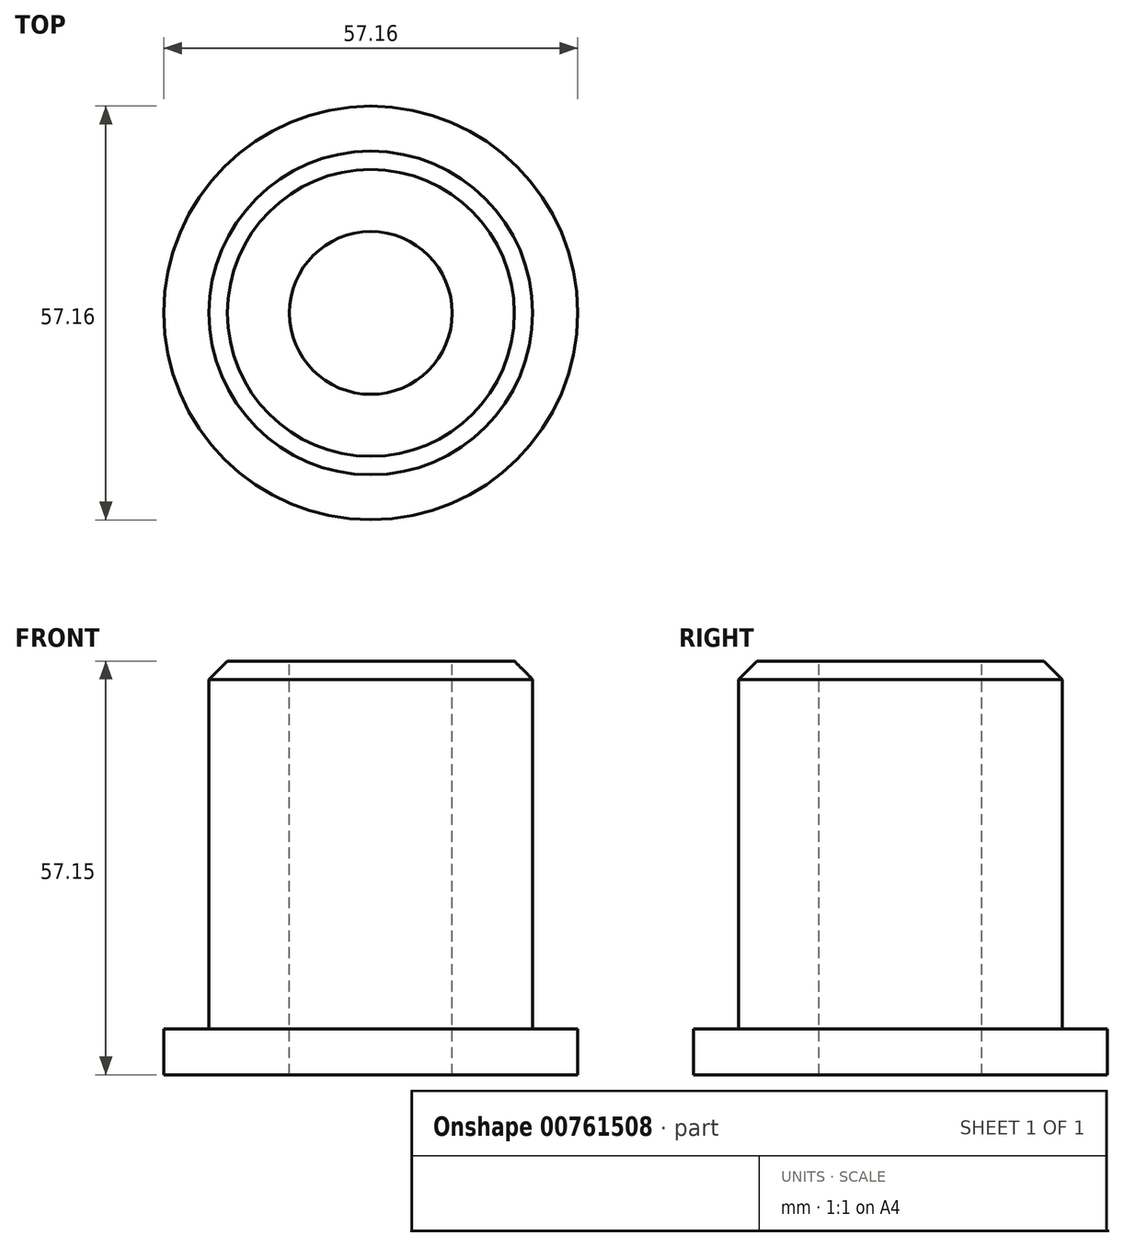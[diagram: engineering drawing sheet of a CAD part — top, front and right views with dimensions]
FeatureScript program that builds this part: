
annotation { "Feature Type Name" : "Feature", "Feature Type Description" : "" }
export const myFeature = defineFeature(function(context is Context, id is Id, definition is map)
    precondition{}
    {
        {
            var Q0;
            Q0=qCreatedBy(makeId("Top.planeOp"),FACE);
            var sketch = newSketch(context, id + "F0", { "sketchPlane" : qUnion([Q0])});
            skCircle(sketch, "E0", {"center": v(0, 0) * mm, "radius": 28.58 * mm});
            skSolve(sketch);
        }
        {
            var Q0;
            Q0 = qSketchRegion(id + "F0", true);
            extrude(context, id + "F1", {"entities" : qUnion([Q0]), "depth" : 6.35 * mm, "offsetDistance" : 25.4 * mm});
        }
        {
            var Q0;
            Q0=makeQuery(id+"F1.opExtrude","CAP_FACE",FACE,{"disambiguationData":[OSD([sQuery(id+"F0.wireOp",EDGE,"E0")])],"isStart":false});
            var sketch = newSketch(context, id + "F2", { "sketchPlane" : qUnion([Q0])});
            skCircle(sketch, "E1", {"center": v(0, 0) * mm, "radius": 22.35 * mm});
            skSolve(sketch);
        }
        {
            var Q0;
            Q0 = qSketchRegion(id + "F2", true);
            extrude(context, id + "F3", {"entities" : qUnion([Q0]), "operationType" : NewBodyOperationType.ADD, "depth" : 50.8 * mm, "offsetDistance" : 25.4 * mm});
        }
        {
            var Q0;
            Q0=makeQuery(id+"F3.opExtrude","CAP_FACE",FACE,{"disambiguationData":[OSD([sQuery(id+"F2.wireOp",EDGE,"E1")])],"isStart":false});
            var sketch = newSketch(context, id + "F4", { "sketchPlane" : qUnion([Q0])});
            skCircle(sketch, "E2", {"center": v(0, 0) * mm, "radius": 11.24 * mm});
            skSolve(sketch);
        }
        {
            var Q0;
            Q0 = qSketchRegion(id + "F4", true);
            extrude(context, id + "F5", {"entities" : qUnion([Q0]), "operationType" : NewBodyOperationType.REMOVE, "endBound" : BoundingType.THROUGH_ALL, "oppositeDirection" : true, "depth" : 25.4 * mm, "offsetDistance" : 25.4 * mm});
        }
        {
            var Q0;
            Q0=makeQuery(id+"F3.opExtrude","CAP_EDGE",EDGE,{"disambiguationData":[OSD([sQuery(id+"F2.wireOp",EDGE,"E1")])],"isStart":false});
            chamfer(context, id + "F6", {"entities" : qUnion([Q0]), "width" : 2.54 * mm, "tangentPropagation" : true});
        }
    });
